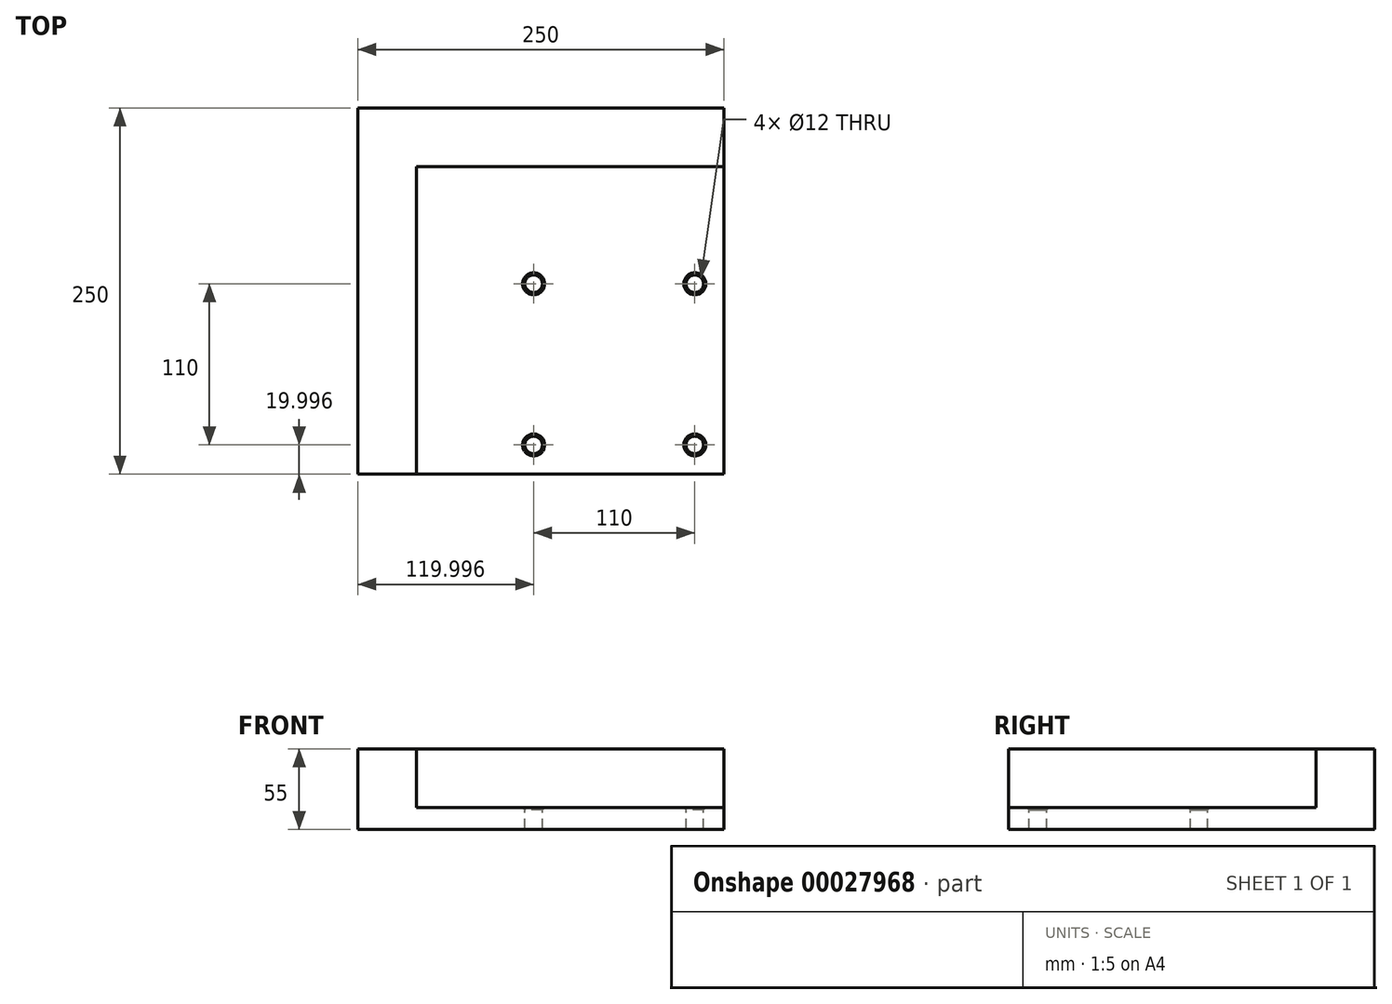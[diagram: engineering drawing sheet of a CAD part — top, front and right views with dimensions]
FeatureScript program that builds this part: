
annotation { "Feature Type Name" : "Feature", "Feature Type Description" : "" }
export const myFeature = defineFeature(function(context is Context, id is Id, definition is map)
    precondition{}
    {
        {
            var Q0;
            Q0=qCreatedBy(makeId("Top.planeOp"),FACE);
            var sketch = newSketch(context, id + "F0", { "sketchPlane" : qUnion([Q0])});
            skLineSegment(sketch, "E0.bottom", {"start": v(-165.67, 147.08) * mm, "end": v(84.33, 147.08) * mm});
            skLineSegment(sketch, "E0.top", {"start": v(-165.67, -102.92) * mm, "end": v(84.33, -102.92) * mm});
            skLineSegment(sketch, "E0.left", {"start": v(-165.67, 147.08) * mm, "end": v(-165.67, -102.92) * mm});
            skLineSegment(sketch, "E0.right", {"start": v(84.33, 147.08) * mm, "end": v(84.33, -102.92) * mm});
            skSolve(sketch);
        }
        {
            var Q0;
            Q0=makeQuery(id+"F0.imprint","IMPRINT",FACE,{"disambiguationData":[TD([[makeQuery(id+"F0.imprint","IMPRINT",EDGE,{"derivedFrom":sQuery(id+"F0.wireOp",EDGE,"E0.bottom")}),-1.0]])]});
            extrude(context, id + "F1", {"entities" : qUnion([Q0]), "depth" : 15 * mm});
        }
        {
            var Q0;
            Q0=makeQuery(id+"F1.opExtrude","CAP_FACE",FACE,{"disambiguationData":[OSD([sQuery(id+"F0.wireOp",EDGE,"E0.bottom"),sQuery(id+"F0.wireOp",EDGE,"E0.top"),sQuery(id+"F0.wireOp",EDGE,"E0.left"),sQuery(id+"F0.wireOp",EDGE,"E0.right")])],"isStart":false});
            var sketch = newSketch(context, id + "F2", { "sketchPlane" : qUnion([Q0])});
            skLineSegment(sketch, "E1.bottom", {"start": v(-165.67, 147.08) * mm, "end": v(-125.67, 147.08) * mm});
            skLineSegment(sketch, "E1.top", {"start": v(-165.67, -102.92) * mm, "end": v(-125.67, -102.92) * mm});
            skLineSegment(sketch, "E1.left", {"start": v(-165.67, 147.08) * mm, "end": v(-165.67, -102.92) * mm});
            skLineSegment(sketch, "E1.right", {"start": v(-125.67, 147.08) * mm, "end": v(-125.67, -102.92) * mm});
            skLineSegment(sketch, "E2.bottom", {"start": v(-125.67, 147.08) * mm, "end": v(84.33, 147.08) * mm});
            skLineSegment(sketch, "E2.top", {"start": v(-125.67, 107.08) * mm, "end": v(84.33, 107.08) * mm});
            skLineSegment(sketch, "E2.left", {"start": v(-125.67, 147.08) * mm, "end": v(-125.67, 107.08) * mm});
            skLineSegment(sketch, "E2.right", {"start": v(84.33, 147.08) * mm, "end": v(84.33, 107.08) * mm});
            skSolve(sketch);
        }
        {
            var Q0;
            Q0=makeQuery(id+"F2.imprint","IMPRINT",FACE,{"disambiguationData":[TD([[makeQuery(id+"F2.imprint","IMPRINT",EDGE,{"derivedFrom":sQuery(id+"F2.wireOp",EDGE,"E2.bottom")}),-1.0]])]});
            var Q1;
            Q1=makeQuery(id+"F2.imprint","IMPRINT",FACE,{"disambiguationData":[TD([[makeQuery(id+"F2.imprint","IMPRINT",EDGE,{"derivedFrom":sQuery(id+"F2.wireOp",EDGE,"E1.bottom")}),-1.0]])]});
            extrude(context, id + "F3", {"entities" : qUnion([Q0, Q1]), "operationType" : NewBodyOperationType.ADD, "depth" : 40 * mm});
        }
        {
            var Q0;
            Q0=makeQuery(id+"F1.opExtrude","CAP_FACE",FACE,{"disambiguationData":[OSD([sQuery(id+"F0.wireOp",EDGE,"E0.bottom"),sQuery(id+"F0.wireOp",EDGE,"E0.top"),sQuery(id+"F0.wireOp",EDGE,"E0.left"),sQuery(id+"F0.wireOp",EDGE,"E0.right")])],"isStart":false});
            var sketch = newSketch(context, id + "F4", { "sketchPlane" : qUnion([Q0])});
            skCircle(sketch, "E3", {"center": v(64.33, -82.92) * mm, "radius": 6 * mm});
            skCircle(sketch, "E4", {"center": v(-45.67, -82.92) * mm, "radius": 6 * mm});
            skCircle(sketch, "E5", {"center": v(-45.67, 27.08) * mm, "radius": 6 * mm});
            skCircle(sketch, "E6", {"center": v(64.33, 27.08) * mm, "radius": 6 * mm});
            skSolve(sketch);
        }
        {
            var Q0;
            Q0=sQuery(id+"F4.wireOp",VERTEX,"E3.center");
            var Q1;
            Q1=sQuery(id+"F4.wireOp",VERTEX,"E5.center");
            var Q2;
            Q2=sQuery(id+"F4.wireOp",VERTEX,"E6.center");
            var Q3;
            Q3=sQuery(id+"F4.wireOp",VERTEX,"E4.center");
            var Q4;
            Q4=makeQuery(id+"F1.opExtrude","SWEPT_BODY",BODY,{"disambiguationData":[OSD([sQuery(id+"F0.wireOp",EDGE,"E0.bottom"),sQuery(id+"F0.wireOp",EDGE,"E0.top"),sQuery(id+"F0.wireOp",EDGE,"E0.left"),sQuery(id+"F0.wireOp",EDGE,"E0.right")])]});
            hole(context, id + "F5", {"style" : HoleStyle.C_SINK, "holeDiameter" : 12 * mm, "cSinkDiameter" : 15 * mm, "endStyle" : HoleEndStyle.THROUGH, "locations" : qUnion([Q0, Q1, Q2, Q3]), "scope" : qUnion([Q4]), "cSinkAngle" : 90 * degree});
        }
    });
